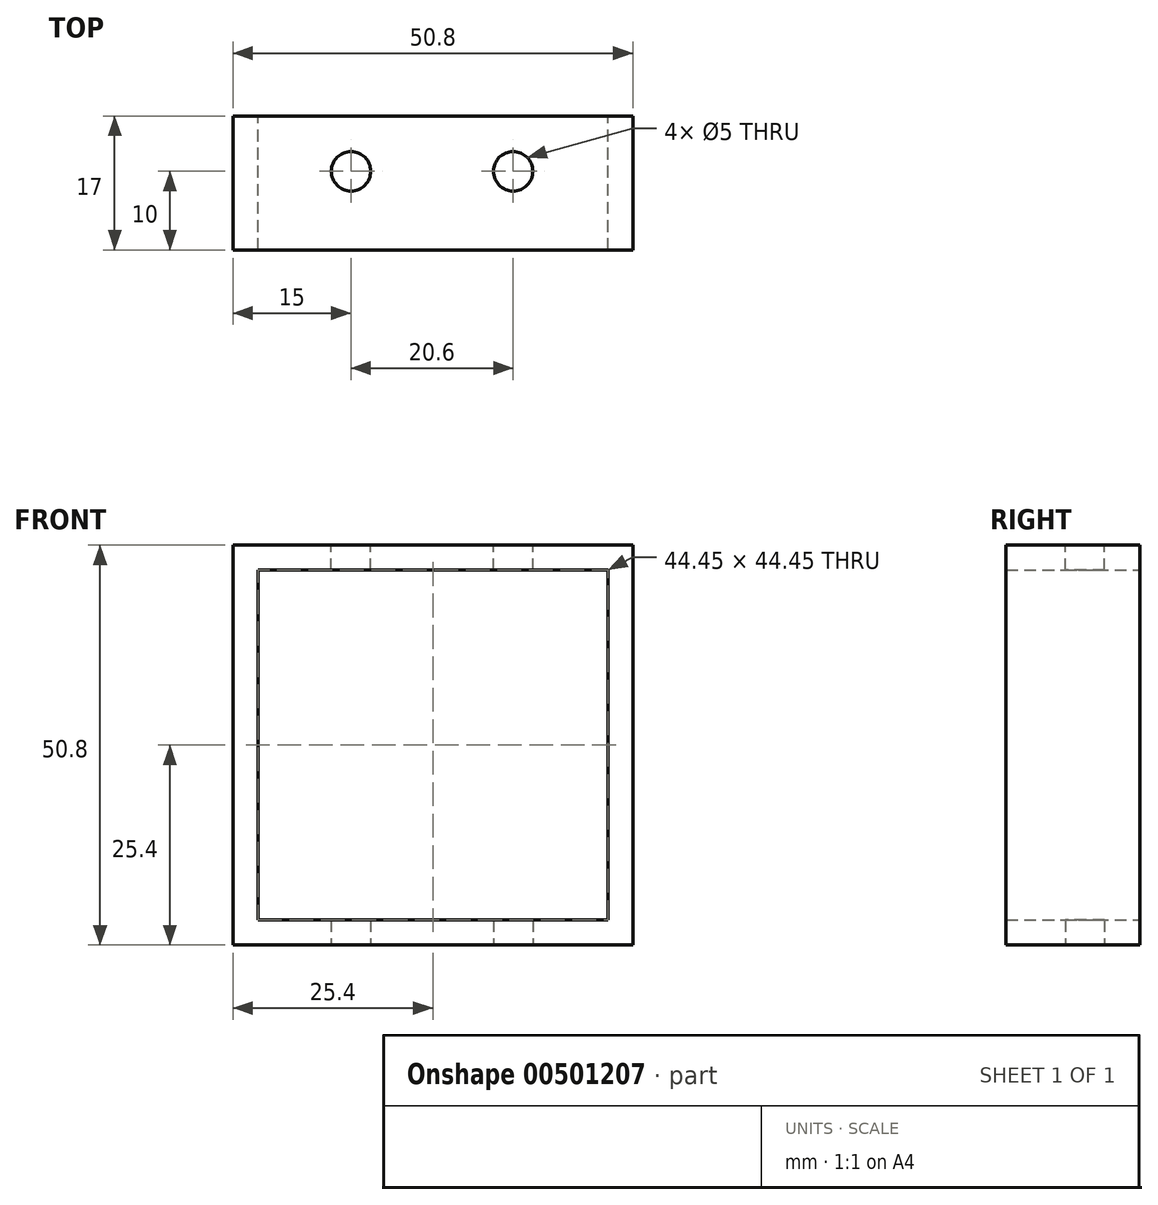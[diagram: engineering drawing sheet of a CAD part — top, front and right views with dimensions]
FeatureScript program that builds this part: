
annotation { "Feature Type Name" : "Feature", "Feature Type Description" : "" }
export const myFeature = defineFeature(function(context is Context, id is Id, definition is map)
    precondition{}
    {
        {
            var Q0;
            Q0=qCreatedBy(makeId("Front.planeOp"),FACE);
            var sketch = newSketch(context, id + "F0", { "sketchPlane" : qUnion([Q0])});
            skLineSegment(sketch, "E0.bottom", {"start": v(-22.22, 22.23) * mm, "end": v(22.22, 22.22) * mm});
            skLineSegment(sketch, "E0.top", {"start": v(-22.22, -22.22) * mm, "end": v(22.22, -22.23) * mm});
            skLineSegment(sketch, "E0.left", {"start": v(-22.22, 22.23) * mm, "end": v(-22.22, -22.23) * mm});
            skLineSegment(sketch, "E0.right", {"start": v(22.23, 22.23) * mm, "end": v(22.23, -22.23) * mm});
            skLineSegment(sketch, "E1.bottom", {"start": v(-25.4, 25.4) * mm, "end": v(25.4, 25.4) * mm});
            skLineSegment(sketch, "E1.top", {"start": v(-25.4, -25.4) * mm, "end": v(25.4, -25.4) * mm});
            skLineSegment(sketch, "E1.left", {"start": v(-25.4, 25.4) * mm, "end": v(-25.4, -25.4) * mm});
            skLineSegment(sketch, "E1.right", {"start": v(25.4, 25.4) * mm, "end": v(25.4, -25.4) * mm});
            skSolve(sketch);
        }
        {
            var Q0;
            Q0 = qSketchRegion(id + "F0", true);
            extrude(context, id + "F1", {"entities" : qUnion([Q0]), "flatOperationType" : FlatOperationType.REMOVE, "depth" : 10 * mm, "offsetDistance" : 25 * mm, "hasSecondDirection" : true, "secondDirectionOppositeDirection" : true, "secondDirectionDepth" : 7 * mm, "domain" : OperationDomain.MODEL});
        }
        {
            var Q0;
            Q0=qCreatedBy(makeId("Top.planeOp"),FACE);
            var sketch = newSketch(context, id + "F2", { "sketchPlane" : qUnion([Q0])});
            skPoint(sketch, "E2", {"position": v(-10.4, 0) * mm});
            skPoint(sketch, "E3", {"position": v(10.2, 0) * mm});
            skSolve(sketch);
        }
        {
            var Q0;
            Q0=sQuery(id+"F2.wireOp",VERTEX,"E2");
            var Q1;
            Q1=sQuery(id+"F2.wireOp",VERTEX,"E3");
            var Q2;
            Q2=sQuery(id+"F2.wireOp",VERTEX,"d77f4220-654e-447b-b4d5-e8e8decdd908");
            var Q3;
            Q3=sQuery(id+"F2.wireOp",VERTEX,"1700266b-4ade-41ff-9f10-a267e81cbd01");
            var Q4;
            Q4=makeQuery(id+"F1.opExtrude","SWEPT_BODY",BODY,{"disambiguationData":[OSD([sQuery(id+"F0.wireOp",EDGE,"E0.bottom"),sQuery(id+"F0.wireOp",EDGE,"E0.top"),sQuery(id+"F0.wireOp",EDGE,"E0.left"),sQuery(id+"F0.wireOp",EDGE,"E0.right"),sQuery(id+"F0.wireOp",EDGE,"E1.bottom"),sQuery(id+"F0.wireOp",EDGE,"E1.top"),sQuery(id+"F0.wireOp",EDGE,"E1.left"),sQuery(id+"F0.wireOp",EDGE,"E1.right")])]});
            hole(context, id + "F3", {"style" : HoleStyle.SIMPLE, "endStyle" : HoleEndStyle.THROUGH, "oppositeDirection" : true, "standardTappedOrClearance" : lookupTablePath({ "standard" : "ISO", "size" : "5", "type" : "Drilled" }), "standardBlindInLast" : lookupTablePath({ "standard" : "ISO", "size" : "5", "type" : "Drilled" }), "holeDiameter" : 5 * mm, "majorDiameter" : 5 * mm, "isTappedThrough" : true, "tappedDepth" : 1 * mm, "tapClearance" : 3, "locations" : qUnion([Q0, Q1, Q2, Q3]), "scope" : qUnion([Q4]), "startStyle" : HoleStartStyle.PART});
        }
        {
            var Q0;
            Q0=sQuery(id+"F2.wireOp",VERTEX,"1700266b-4ade-41ff-9f10-a267e81cbd01");
            var Q1;
            Q1=sQuery(id+"F2.wireOp",VERTEX,"E2");
            var Q2;
            Q2=sQuery(id+"F2.wireOp",VERTEX,"d77f4220-654e-447b-b4d5-e8e8decdd908");
            var Q3;
            Q3=sQuery(id+"F2.wireOp",VERTEX,"E3");
            var Q4;
            Q4=makeQuery(id+"F1.opExtrude","SWEPT_BODY",BODY,{"disambiguationData":[OSD([sQuery(id+"F0.wireOp",EDGE,"E0.bottom"),sQuery(id+"F0.wireOp",EDGE,"E0.top"),sQuery(id+"F0.wireOp",EDGE,"E0.left"),sQuery(id+"F0.wireOp",EDGE,"E0.right"),sQuery(id+"F0.wireOp",EDGE,"E1.bottom"),sQuery(id+"F0.wireOp",EDGE,"E1.top"),sQuery(id+"F0.wireOp",EDGE,"E1.left"),sQuery(id+"F0.wireOp",EDGE,"E1.right")])]});
            hole(context, id + "F4", {"style" : HoleStyle.SIMPLE, "endStyle" : HoleEndStyle.THROUGH, "standardTappedOrClearance" : lookupTablePath({ "standard" : "ISO", "size" : "5", "type" : "Drilled" }), "standardBlindInLast" : lookupTablePath({ "standard" : "ISO", "size" : "5", "type" : "Drilled" }), "holeDiameter" : 5 * mm, "majorDiameter" : 5 * mm, "isTappedThrough" : true, "tappedDepth" : 1 * mm, "tapClearance" : 3, "locations" : qUnion([Q0, Q1, Q2, Q3]), "scope" : qUnion([Q4]), "startStyle" : HoleStartStyle.PART});
        }
    });
